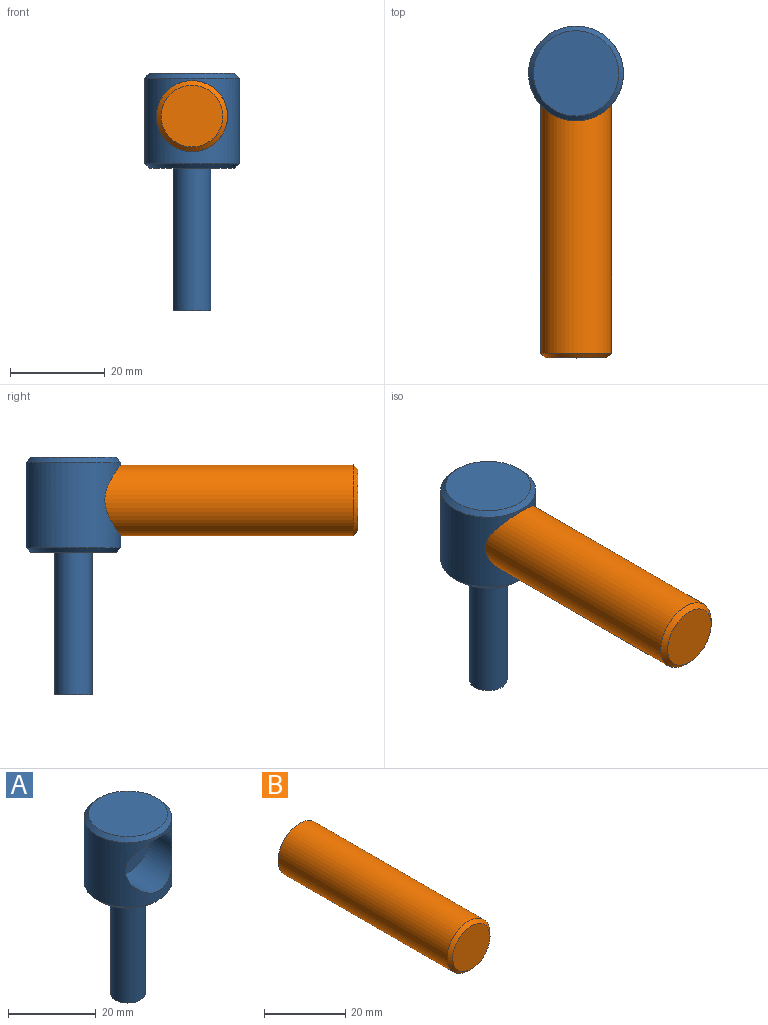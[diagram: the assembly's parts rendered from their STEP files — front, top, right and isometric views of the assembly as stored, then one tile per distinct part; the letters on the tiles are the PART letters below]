
ASSEMBLY  parts=2 mates=1
PART A: 9 faces, bbox 20x20x50 mm
  f0: cylinder r=10mm len=20mm, axis (0,0,-1), area 937.8mm2, adj f5,f6,f7
  f1: plane 8x8mm, normal (0,0,-1), area 50.3mm2, adj f4
  f2: plane 18x18mm, normal (0,0,1), area 254.5mm2, adj f6
  f3: plane 18x18mm, normal (0,0,-1), area 204.2mm2, adj f4,f5
  f4: cylinder r=4mm len=30mm, axis (0,0,-1), area 754mm2, adj f1,f3
  f5: cone r=9mm half-angle=45deg, axis (0,0,1), area 84.4mm2, adj f0,f3
  f6: cone r=10mm half-angle=45deg, axis (0,0,-1), area 84.4mm2, adj f0,f2
  f7: cylinder r=7.5mm len=15mm, axis (0,1,0), area 395.5mm2, adj f0,f8
  f8: plane 15x15mm, normal (0,-1,0), area 176.7mm2, adj f7
PART B: 4 faces, bbox 15x60x15 mm
  f0: cylinder r=7.5mm len=59mm, axis (0,1,0), area 2780.3mm2, adj f2,f3
  f1: plane 13x13mm, normal (0,-1,0), area 132.7mm2, adj f3
  f2: plane 15x15mm, normal (0,1,0), area 176.7mm2, adj f0
  f3: cone r=6.5mm half-angle=45deg, axis (0,1,0), area 62.2mm2, adj f0,f1
PLACE A at identity fixed
PLACE B at identity
MATE fastened B.f0 <-> A.f7  axis (0,1,0) through (0,0,11)mm
